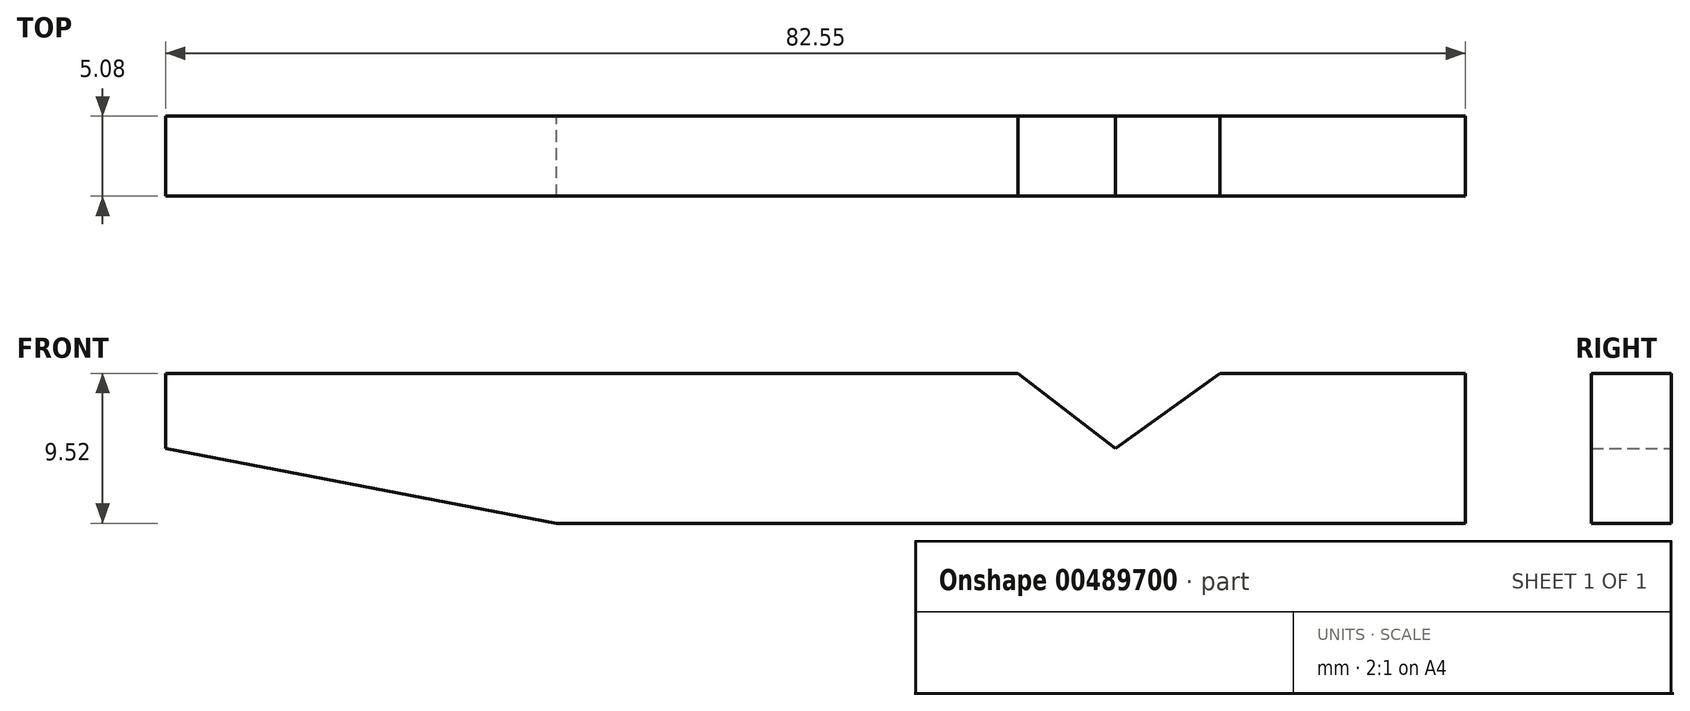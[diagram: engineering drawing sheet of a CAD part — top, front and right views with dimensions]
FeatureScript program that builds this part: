
annotation { "Feature Type Name" : "Feature", "Feature Type Description" : "" }
export const myFeature = defineFeature(function(context is Context, id is Id, definition is map)
    precondition{}
    {
        {
            var Q0;
            Q0=qCreatedBy(makeId("Front.planeOp"),FACE);
            var sketch = newSketch(context, id + "F0", { "sketchPlane" : qUnion([Q0])});
            skLineSegment(sketch, "E0.bottom", {"start": v(41.28, -4.76) * mm, "end": v(-16.46, -4.76) * mm});
            skLineSegment(sketch, "E0.top", {"start": v(41.28, 4.76) * mm, "end": v(25.68, 4.76) * mm});
            skLineSegment(sketch, "E0.left", {"start": v(41.28, -4.76) * mm, "end": v(41.28, 4.76) * mm});
            skLineSegment(sketch, "E0.right", {"start": v(-41.28, 0) * mm, "end": v(-41.28, 4.76) * mm});
            skPoint(sketch, "E0.middle", {"position": v(0, 0) * mm});
            skLineSegment(sketch, "E1", {"start": v(19.05, 0) * mm, "end": v(41.28, 0) * mm});
            skPoint(sketch, "E1.startSnap0", {"position": v(41.28, 0) * mm});
            skLineSegment(sketch, "E2", {"start": v(19.05, 0) * mm, "end": v(25.68, 4.76) * mm});
            skLineSegment(sketch, "E3", {"start": v(19.05, 0) * mm, "end": v(12.84, 4.76) * mm});
            skLineSegment(sketch, "E4.trimOffspring", {"start": v(12.84, 4.76) * mm, "end": v(-41.28, 4.76) * mm});
            skLineSegment(sketch, "E5", {"start": v(-41.28, 0) * mm, "end": v(-16.46, -4.76) * mm});
            skPoint(sketch, "E6.orphan", {"position": v(-41.28, -4.76) * mm});
            skSolve(sketch);
        }
        {
            var Q0;
            {var subQ1=sQuery(id+"F0.wireOp",EDGE,"E0.bottom");Q0=makeQuery(id+"F0.imprint","IMPRINT",FACE,{"disambiguationData":[TD([[makeQuery(id+"F0.imprint","IMPRINT",EDGE,{"derivedFrom":subQ1}),-1.0]])]});}
            var Q1;
            {var subQ0=sQuery(id+"F0.wireOp",EDGE,"E0.top");Q1=makeQuery(id+"F0.imprint","IMPRINT",FACE,{"disambiguationData":[TD([[makeQuery(id+"F0.imprint","IMPRINT",EDGE,{"derivedFrom":subQ0}),1.0]])]});}
            extrude(context, id + "F1", {"entities" : qUnion([Q0, Q1]), "depth" : 5.08 * mm});
        }
    });
